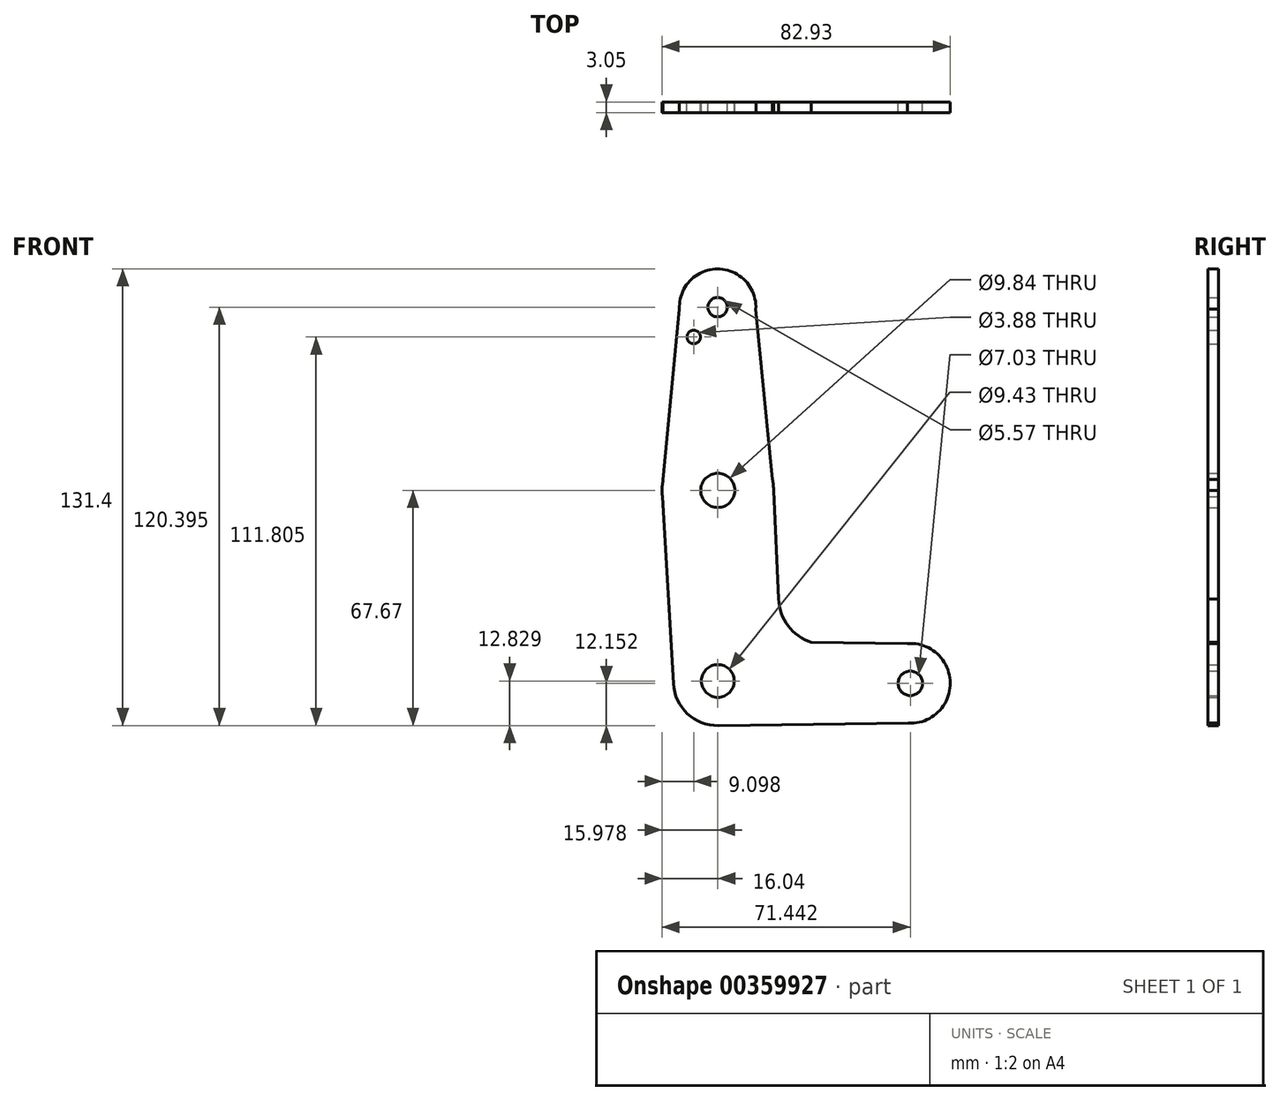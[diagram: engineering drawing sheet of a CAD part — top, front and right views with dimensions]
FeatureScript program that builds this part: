
annotation { "Feature Type Name" : "Feature", "Feature Type Description" : "" }
export const myFeature = defineFeature(function(context is Context, id is Id, definition is map)
    precondition{}
    {
        {
            var Q0;
            Q0=qCreatedBy(makeId("Front.planeOp"),FACE);
            var sketch = newSketch(context, id + "F0", { "sketchPlane" : qUnion([Q0])});
            skCircle(sketch, "E0", {"center": v(0, -54.84) * mm, "radius": 12.83 * mm});
            skArc(sketch, "E1", {"start": v(17.52, -31.23) * mm, "mid": v(20.21, -38.98) * mm, "end": v(26.92, -43.7) * mm});
            skLineSegment(sketch, "E2", {"start": v(56.24, -66.98) * mm, "end": v(0, -67.68) * mm});
            skCircle(sketch, "E3", {"center": v(55.4, -55.52) * mm, "radius": 11.49 * mm});
            skLineSegment(sketch, "E4", {"start": v(54.57, -44.06) * mm, "end": v(26.92, -43.7) * mm});
            skCircle(sketch, "E5", {"center": v(-0.06, 52.73) * mm, "radius": 2.79 * mm});
            skCircle(sketch, "E6", {"center": v(0, 0) * mm, "radius": 4.92 * mm});
            skCircle(sketch, "E7", {"center": v(0, -54.84) * mm, "radius": 4.71 * mm});
            skCircle(sketch, "E8", {"center": v(55.4, -55.52) * mm, "radius": 3.52 * mm});
            skCircle(sketch, "E9", {"center": v(-6.94, 44.14) * mm, "radius": 1.94 * mm});
            skLineSegment(sketch, "E10", {"start": v(10.88, 52.73) * mm, "end": v(16.04, 0) * mm});
            skLineSegment(sketch, "E11", {"start": v(16.04, 0) * mm, "end": v(17.52, -31.23) * mm});
            skCircle(sketch, "E12", {"center": v(0, 0) * mm, "radius": 16.04 * mm});
            skCircle(sketch, "E13", {"center": v(-0.06, 52.73) * mm, "radius": 11 * mm});
            skLineSegment(sketch, "E14", {"start": v(-16.04, 0) * mm, "end": v(-10.74, 55.4) * mm});
            skLineSegment(sketch, "E15", {"start": v(-16.04, 0) * mm, "end": v(-12.81, -55.58) * mm});
            skSolve(sketch);
        }
        {
            var Q0;
            Q0 = qSketchRegion(id + "F0", true);
            extrude(context, id + "F1", {"entities" : qUnion([Q0]), "depth" : 3.05 * mm});
        }
    });
